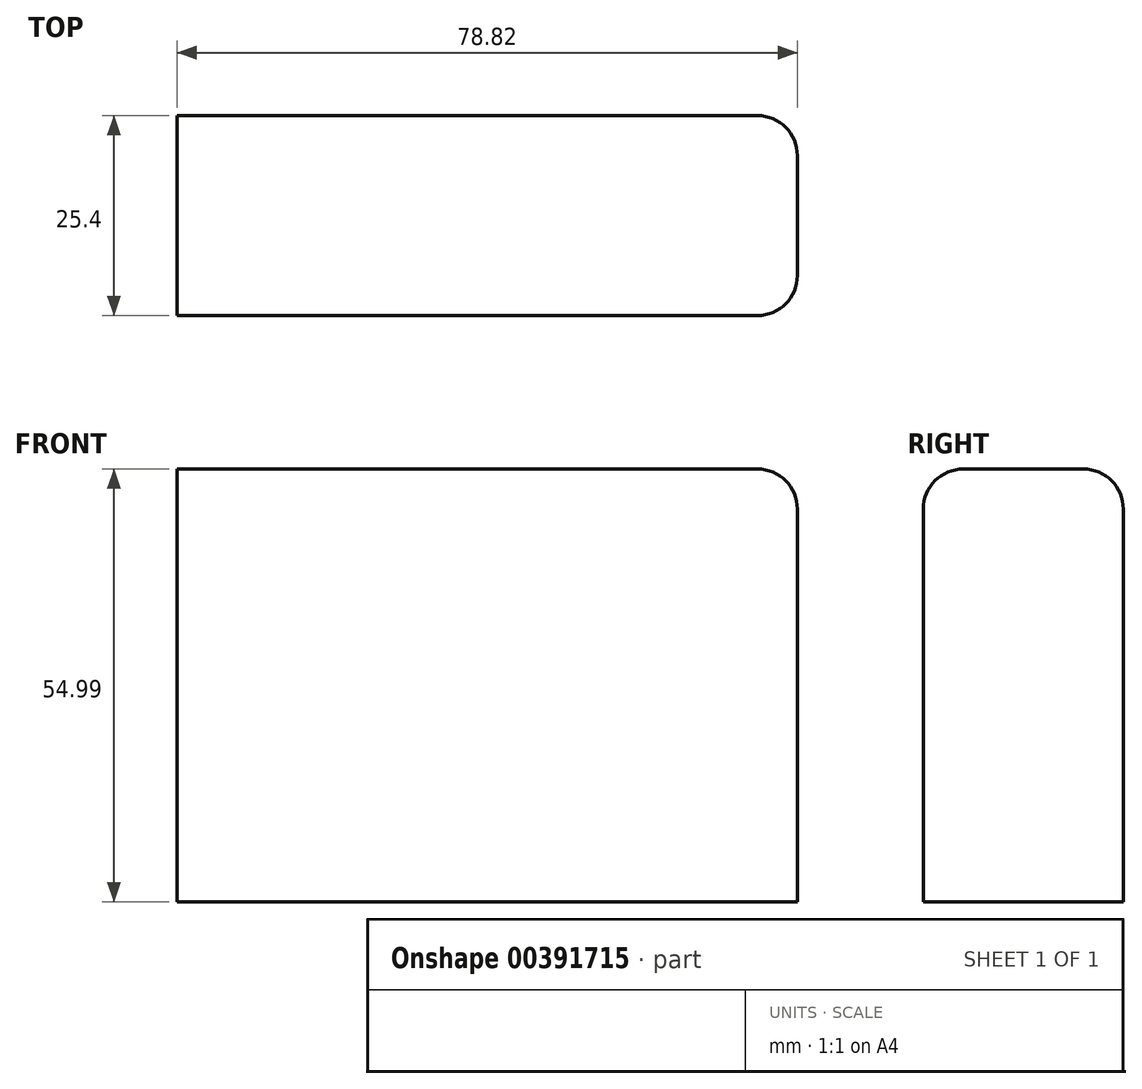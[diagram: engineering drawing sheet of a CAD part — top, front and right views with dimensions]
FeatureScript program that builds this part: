
annotation { "Feature Type Name" : "Feature", "Feature Type Description" : "" }
export const myFeature = defineFeature(function(context is Context, id is Id, definition is map)
    precondition{}
    {
        {
            var Q0;
            Q0=qCreatedBy(makeId("Front.planeOp"),FACE);
            var sketch = newSketch(context, id + "F0", { "sketchPlane" : qUnion([Q0])});
            skLineSegment(sketch, "E0.bottom", {"start": v(-33.36, -32.63) * mm, "end": v(45.46, -32.63) * mm});
            skLineSegment(sketch, "E0.top", {"start": v(-33.36, 22.36) * mm, "end": v(45.46, 22.36) * mm});
            skLineSegment(sketch, "E0.left", {"start": v(-33.36, -32.63) * mm, "end": v(-33.36, 22.36) * mm});
            skLineSegment(sketch, "E0.right", {"start": v(45.46, -32.63) * mm, "end": v(45.46, 22.36) * mm});
            skSolve(sketch);
        }
        {
            var Q0;
            Q0 = qSketchRegion(id + "F0", true);
            extrude(context, id + "F1", {"entities" : qUnion([Q0]), "depth" : 25.4 * mm});
        }
        {
            var Q0;
            Q0=makeQuery(id+"F1.opExtrude","CAP_EDGE",EDGE,{"disambiguationData":[OSD([sQuery(id+"F0.wireOp",EDGE,"E0.top")])],"isStart":false});
            var Q1;
            Q1=makeQuery(id+"F1.opExtrude","CAP_EDGE",EDGE,{"disambiguationData":[OSD([sQuery(id+"F0.wireOp",EDGE,"E0.right")])],"isStart":true});
            var Q2;
            Q2=makeQuery(id+"F1.opExtrude","CAP_EDGE",EDGE,{"disambiguationData":[OSD([sQuery(id+"F0.wireOp",EDGE,"E0.right")])],"isStart":false});
            var Q3;
            Q3=makeQuery(id+"F1.opExtrude","CAP_EDGE",EDGE,{"disambiguationData":[OSD([sQuery(id+"F0.wireOp",EDGE,"E0.top")])],"isStart":true});
            var Q4;
            Q4=makeQuery(id+"F1.opExtrude","SWEPT_EDGE",EDGE,{"disambiguationData":[OSD([sQuery(id+"F0.wireOp",EDGE,"E0.top"),sQuery(id+"F0.wireOp",EDGE,"E0.right")])]});
            fillet(context, id + "F2", {"entities" : qUnion([Q0, Q1, Q2, Q3, Q4]), "radius" : 5.08 * mm, "tangentPropagation" : true, "allowEdgeOverflow" : false});
        }
    });
